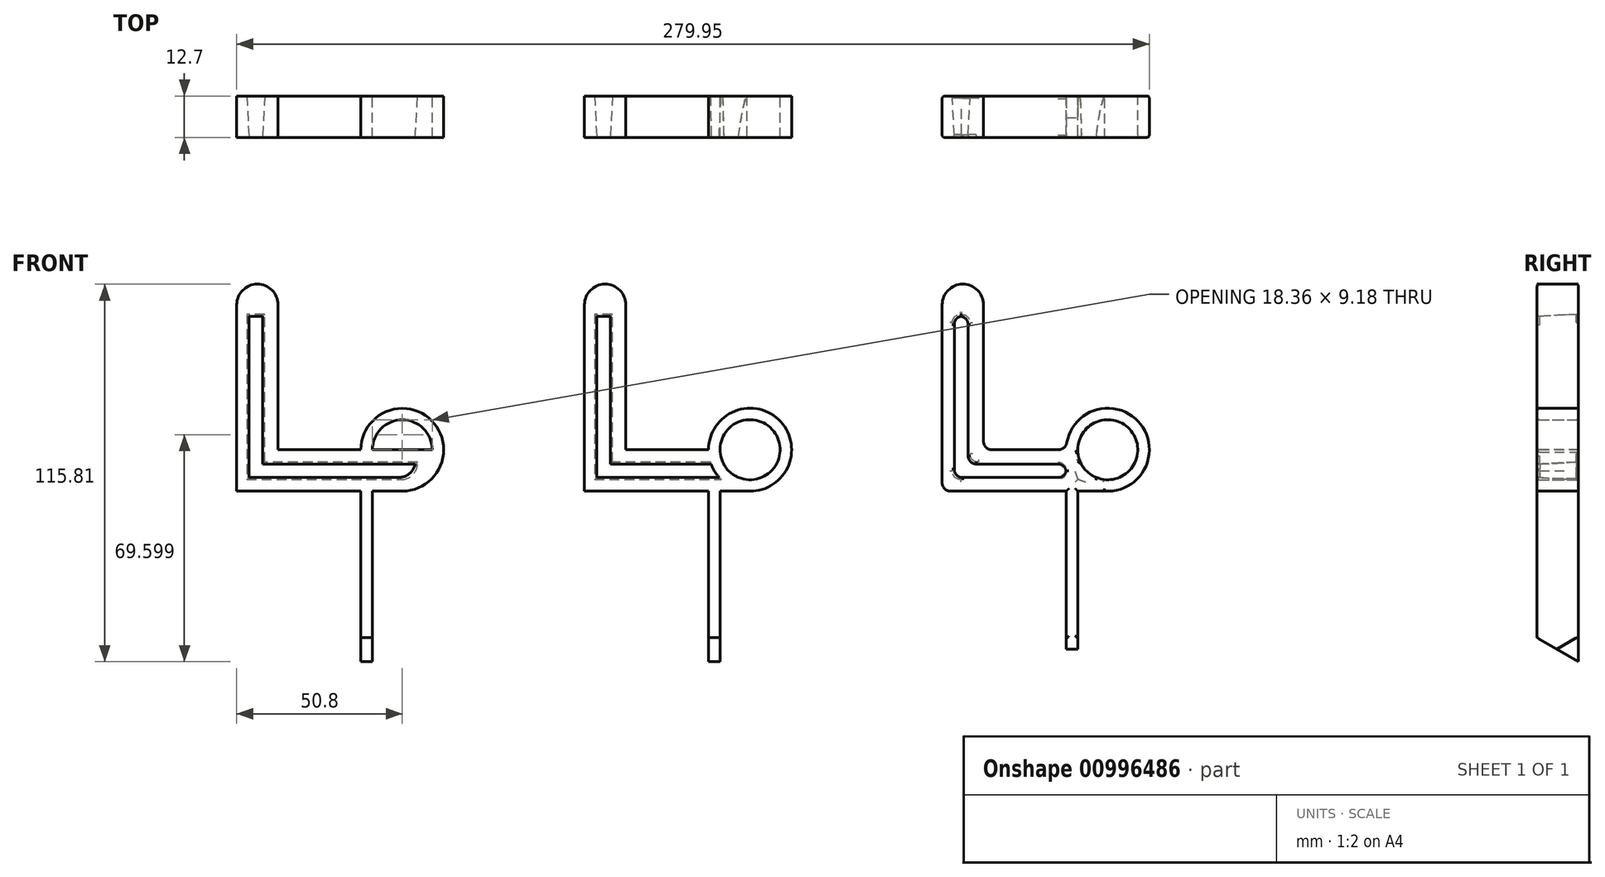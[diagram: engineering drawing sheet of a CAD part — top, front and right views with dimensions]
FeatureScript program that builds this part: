
annotation { "Feature Type Name" : "Feature", "Feature Type Description" : "" }
export const myFeature = defineFeature(function(context is Context, id is Id, definition is map)
    precondition{}
    {
        {
            var Q0;
            Q0=qCreatedBy(makeId("Front.planeOp"),FACE);
            var sketch = newSketch(context, id + "F0", { "sketchPlane" : qUnion([Q0])});
            skLineSegment(sketch, "E0", {"start": v(0, 63.5) * mm, "end": v(0, 0) * mm});
            skLineSegment(sketch, "E1", {"start": v(0, 0) * mm, "end": v(63.5, 0) * mm});
            skLineSegment(sketch, "E2", {"start": v(0, 63.5) * mm, "end": v(12.7, 63.5) * mm});
            skLineSegment(sketch, "E3", {"start": v(12.7, 63.5) * mm, "end": v(12.7, 12.7) * mm});
            skLineSegment(sketch, "E4", {"start": v(12.7, 12.7) * mm, "end": v(63.5, 12.7) * mm});
            skLineSegment(sketch, "E5", {"start": v(63.5, 12.7) * mm, "end": v(63.5, 0) * mm});
            skSolve(sketch);
        }
        {
            var Q0;
            Q0 = qSketchRegion(id + "F0", true);
            extrude(context, id + "F1", {"entities" : qUnion([Q0]), "depth" : 12.7 * mm, "offsetDistance" : 25.4 * mm});
        }
        {
            var Q0;
            Q0=qCreatedBy(makeId("Front.planeOp"),FACE);
            var sketch = newSketch(context, id + "F2", { "sketchPlane" : qUnion([Q0])});
            skArc(sketch, "E6", {"start": v(63.5, 12.7) * mm, "mid": v(50.8, 25.37) * mm, "end": v(38.1, 12.7) * mm});
            skArc(sketch, "E7", {"start": v(38.1, 12.7) * mm, "mid": v(50.8, 0) * mm, "end": v(63.5, 12.7) * mm});
            skCircle(sketch, "E8", {"center": v(50.8, 12.7) * mm, "radius": 9.18 * mm});
            skSolve(sketch);
        }
        {
            var Q0;
            Q0 = qSketchRegion(id + "F2", true);
            var Q1;
            Q1=makeQuery(id+"F1.opExtrude","CAP_VERTEX",VERTEX,{"disambiguationData":[OSD([sQuery(id+"F0.wireOp",EDGE,"E4"),sQuery(id+"F0.wireOp",EDGE,"E5")])],"isStart":false});
            extrude(context, id + "F3", {"entities" : qUnion([Q0]), "operationType" : NewBodyOperationType.ADD, "endBound" : BoundingType.UP_TO_VERTEX, "depth" : 25.4 * mm, "endBoundEntityVertex" : qUnion([Q1]), "offsetDistance" : 25.4 * mm});
        }
        {
            var Q0;
            Q0=qCreatedBy(makeId("Front.planeOp"),FACE);
            var sketch = newSketch(context, id + "F4", { "sketchPlane" : qUnion([Q0])});
            skLineSegment(sketch, "E9.bottom", {"start": v(38.1, 12.7) * mm, "end": v(41.62, 12.7) * mm});
            skLineSegment(sketch, "E9.top", {"start": v(38.1, -57.68) * mm, "end": v(41.62, -57.68) * mm});
            skLineSegment(sketch, "E9.left", {"start": v(38.1, 12.7) * mm, "end": v(38.1, -57.68) * mm});
            skLineSegment(sketch, "E9.right", {"start": v(41.62, 12.7) * mm, "end": v(41.62, -57.68) * mm});
            skSolve(sketch);
        }
        {
            var Q0;
            Q0=makeQuery(id+"F4.imprint","IMPRINT",FACE,{"disambiguationData":[TD([[makeQuery(id+"F4.imprint","IMPRINT",EDGE,{"derivedFrom":sQuery(id+"F4.wireOp",EDGE,"E9.bottom")}),-1.0]])]});
            var Q1;
            Q1=makeQuery(id+"F3.opExtrude","CAP_VERTEX",VERTEX,{"disambiguationData":[OSD([sQuery(id+"F2.wireOp",EDGE,"E6"),sQuery(id+"F2.wireOp",EDGE,"E7")]),OD(1.0)],"isStart":false});
            extrude(context, id + "F5", {"entities" : qUnion([Q0]), "operationType" : NewBodyOperationType.ADD, "endBound" : BoundingType.UP_TO_VERTEX, "depth" : 25.4 * mm, "endBoundEntityVertex" : qUnion([Q1]), "offsetDistance" : 25.4 * mm});
        }
        {
            var Q0;
            Q0=makeQuery(id+"F1.opExtrude","SWEPT_EDGE",EDGE,{"disambiguationData":[OSD([sQuery(id+"F0.wireOp",EDGE,"E2"),sQuery(id+"F0.wireOp",EDGE,"E3")])]});
            var Q1;
            Q1=makeQuery(id+"F1.opExtrude","SWEPT_EDGE",EDGE,{"disambiguationData":[OSD([sQuery(id+"F0.wireOp",EDGE,"E0"),sQuery(id+"F0.wireOp",EDGE,"E2")])]});
            fillet(context, id + "F6", {"entities" : qUnion([Q0, Q1]), "radius" : 6.35 * mm, "tangentPropagation" : true, "allowEdgeOverflow" : false});
        }
        {
            var Q0;
            Q0=makeQuery(id+"F1.opExtrude","SWEPT_EDGE",EDGE,{"disambiguationData":[OSD([sQuery(id+"F0.wireOp",EDGE,"E1"),sQuery(id+"F0.wireOp",EDGE,"E5")])]});
            fillet(context, id + "F7", {"entities" : qUnion([Q0]), "radius" : 12.7 * mm, "tangentPropagation" : true, "allowEdgeOverflow" : false});
        }
        {
            var Q0;
            Q0=makeQuery(id+"F5.opExtrude","CAP_EDGE",EDGE,{"disambiguationData":[OSD([sQuery(id+"F4.wireOp",EDGE,"E9.top")])],"isStart":false});
            chamfer(context, id + "F8", {"entities" : qUnion([Q0]), "chamferType" : ChamferType.OFFSET_ANGLE, "width" : 12.7 * mm, "oppositeDirection" : false, "angle" : 60 * degree, "tangentPropagation" : true});
        }
        {
            var Q0;
            Q0=makeQuery(id+"F5.boolean.opBoolean","MERGE",FACE,{"derivedFrom":[makeQuery(id+"F3.boolean.opBoolean","MERGE",FACE,{"derivedFrom":[makeQuery(id+"F1.opExtrude","CAP_FACE",FACE,{"disambiguationData":[OSD([sQuery(id+"F0.wireOp",EDGE,"E0"),sQuery(id+"F0.wireOp",EDGE,"E1"),sQuery(id+"F0.wireOp",EDGE,"E2"),sQuery(id+"F0.wireOp",EDGE,"E3"),sQuery(id+"F0.wireOp",EDGE,"E4"),sQuery(id+"F0.wireOp",EDGE,"E5")])],"isStart":false}),makeQuery(id+"F3.opExtrude","CAP_FACE",FACE,{"disambiguationData":[OSD([sQuery(id+"F2.wireOp",EDGE,"E6"),sQuery(id+"F2.wireOp",EDGE,"E7"),sQuery(id+"F2.wireOp",EDGE,"E8")])],"isStart":false})]}),makeQuery(id+"F5.opExtrude","CAP_FACE",FACE,{"disambiguationData":[OSD([sQuery(id+"F4.wireOp",EDGE,"E9.bottom"),sQuery(id+"F4.wireOp",EDGE,"E9.top"),sQuery(id+"F4.wireOp",EDGE,"E9.left"),sQuery(id+"F4.wireOp",EDGE,"E9.right")])],"isStart":false})]});
            var sketch = newSketch(context, id + "F9", { "sketchPlane" : qUnion([Q0])});
            skLineSegment(sketch, "E10", {"start": v(7.9, 53.6) * mm, "end": v(7.9, 8.26) * mm});
            skLineSegment(sketch, "E11", {"start": v(7.9, 8.26) * mm, "end": v(54.83, 8.26) * mm});
            skLineSegment(sketch, "E12", {"start": v(54.83, 8.26) * mm, "end": v(54.83, 4.2) * mm});
            skLineSegment(sketch, "E13", {"start": v(54.83, 4.2) * mm, "end": v(3.75, 4.2) * mm});
            skLineSegment(sketch, "E14", {"start": v(3.75, 4.2) * mm, "end": v(3.75, 53.6) * mm});
            skLineSegment(sketch, "E15", {"start": v(3.75, 53.6) * mm, "end": v(7.9, 53.6) * mm});
            skPoint(sketch, "E16.visualSharp", {"position": v(7.9, 53.6) * mm});
            skLineSegment(sketch, "E16.filletArc", {"start": v(7.9, 53.6) * mm, "end": v(7.9, 53.6) * mm});
            skSolve(sketch);
        }
        {
            var Q0;
            Q0 = qSketchRegion(id + "F9", true);
            extrude(context, id + "F10", {"entities" : qUnion([Q0]), "operationType" : NewBodyOperationType.REMOVE, "oppositeDirection" : true, "depth" : 102.36 * mm, "offsetDistance" : 25.4 * mm, "hasDraft" : true, "draftAngle" : 3 * degree});
        }
        {
            var Q0;
            Q0=makeQuery(id+"F10.boolean.opBoolean","COPY",EDGE,{"derivedFrom":makeQuery(id+"F10.opExtrude","SWEPT_EDGE",EDGE,{"disambiguationData":[OSD([sQuery(id+"F9.wireOp",EDGE,"E12"),sQuery(id+"F9.wireOp",EDGE,"E13")])]})});
            fillet(context, id + "F11", {"entities" : qUnion([Q0]), "radius" : 5.08 * mm, "tangentPropagation" : true, "allowEdgeOverflow" : false});
        }
        {
            var Q0;
            Q0=makeQuery(id+"F1.opExtrude","SWEPT_BODY",BODY,{"disambiguationData":[OSD([sQuery(id+"F0.wireOp",EDGE,"E0"),sQuery(id+"F0.wireOp",EDGE,"E1"),sQuery(id+"F0.wireOp",EDGE,"E2"),sQuery(id+"F0.wireOp",EDGE,"E3"),sQuery(id+"F0.wireOp",EDGE,"E4"),sQuery(id+"F0.wireOp",EDGE,"E5")])]});
            transform(context, id + "F12", {"entities" : qUnion([Q0]), "transformType" : TransformType.TRANSLATION_3D, "dx" : 106.68 * mm, "dy" : 0 * mm, "dz" : 0 * mm, "makeCopy" : true});
        }
        {
            var Q0;
            Q0=qCreatedBy(makeId("Front.planeOp"),FACE);
            var sketch = newSketch(context, id + "F13", { "sketchPlane" : qUnion([Q0])});
            skCircle(sketch, "E17", {"center": v(157.48, 12.7) * mm, "radius": 9.21 * mm});
            skSolve(sketch);
        }
        {
            var Q0;
            Q0 = qSketchRegion(id + "F13", true);
            extrude(context, id + "F14", {"entities" : qUnion([Q0]), "operationType" : NewBodyOperationType.REMOVE, "depth" : 103.12 * mm, "offsetDistance" : 25.4 * mm});
        }
        {
            var Q0;
            Q0=makeQuery(id+"F12.opPattern","COPY",FACE,{"derivedFrom":makeQuery(id+"F5.boolean.opBoolean","MERGE",FACE,{"derivedFrom":[makeQuery(id+"F3.boolean.opBoolean","MERGE",FACE,{"derivedFrom":[makeQuery(id+"F1.opExtrude","CAP_FACE",FACE,{"disambiguationData":[OSD([sQuery(id+"F0.wireOp",EDGE,"E0"),sQuery(id+"F0.wireOp",EDGE,"E1"),sQuery(id+"F0.wireOp",EDGE,"E2"),sQuery(id+"F0.wireOp",EDGE,"E3"),sQuery(id+"F0.wireOp",EDGE,"E4"),sQuery(id+"F0.wireOp",EDGE,"E5")])],"isStart":false}),makeQuery(id+"F3.opExtrude","CAP_FACE",FACE,{"disambiguationData":[OSD([sQuery(id+"F2.wireOp",EDGE,"E6"),sQuery(id+"F2.wireOp",EDGE,"E7"),sQuery(id+"F2.wireOp",EDGE,"E8")])],"isStart":false})]}),makeQuery(id+"F5.opExtrude","CAP_FACE",FACE,{"disambiguationData":[OSD([sQuery(id+"F4.wireOp",EDGE,"E9.bottom"),sQuery(id+"F4.wireOp",EDGE,"E9.top"),sQuery(id+"F4.wireOp",EDGE,"E9.left"),sQuery(id+"F4.wireOp",EDGE,"E9.right")])],"isStart":false})]}),"instanceName":"1"});
            var sketch = newSketch(context, id + "F15", { "sketchPlane" : qUnion([Q0])});
            skCircle(sketch, "E18", {"center": v(157.48, 12.7) * mm, "radius": 12.74 * mm});
            skCircle(sketch, "E19", {"center": v(157.48, 12.7) * mm, "radius": 9.23 * mm});
            skSolve(sketch);
        }
        {
            var Q0;
            Q0 = qSketchRegion(id + "F15", true);
            extrude(context, id + "F16", {"entities" : qUnion([Q0]), "operationType" : NewBodyOperationType.ADD, "oppositeDirection" : true, "depth" : 12.7 * mm, "offsetDistance" : 25.4 * mm});
        }
        {
            var Q0;
            Q0=makeQuery(id+"F12.opPattern","COPY",BODY,{"derivedFrom":makeQuery(id+"F1.opExtrude","SWEPT_BODY",BODY,{"disambiguationData":[OSD([sQuery(id+"F0.wireOp",EDGE,"E0"),sQuery(id+"F0.wireOp",EDGE,"E1"),sQuery(id+"F0.wireOp",EDGE,"E2"),sQuery(id+"F0.wireOp",EDGE,"E3"),sQuery(id+"F0.wireOp",EDGE,"E4"),sQuery(id+"F0.wireOp",EDGE,"E5")])]}),"instanceName":"1"});
            transform(context, id + "F17", {"entities" : qUnion([Q0]), "transformType" : TransformType.TRANSLATION_3D, "dx" : 109.73 * mm, "dy" : 0 * mm, "dz" : 0 * mm, "makeCopy" : true});
        }
        {
            var Q0;
            Q0=makeQuery(id+"F17.opPattern","COPY",FACE,{"derivedFrom":makeQuery(id+"F16.boolean.opBoolean","MERGE",FACE,{"derivedFrom":[makeQuery(id+"F12.opPattern","COPY",FACE,{"derivedFrom":makeQuery(id+"F5.boolean.opBoolean","MERGE",FACE,{"derivedFrom":[makeQuery(id+"F3.boolean.opBoolean","MERGE",FACE,{"derivedFrom":[makeQuery(id+"F1.opExtrude","CAP_FACE",FACE,{"disambiguationData":[OSD([sQuery(id+"F0.wireOp",EDGE,"E0"),sQuery(id+"F0.wireOp",EDGE,"E1"),sQuery(id+"F0.wireOp",EDGE,"E2"),sQuery(id+"F0.wireOp",EDGE,"E3"),sQuery(id+"F0.wireOp",EDGE,"E4"),sQuery(id+"F0.wireOp",EDGE,"E5")])],"isStart":false}),makeQuery(id+"F3.opExtrude","CAP_FACE",FACE,{"disambiguationData":[OSD([sQuery(id+"F2.wireOp",EDGE,"E6"),sQuery(id+"F2.wireOp",EDGE,"E7"),sQuery(id+"F2.wireOp",EDGE,"E8")])],"isStart":false})]}),makeQuery(id+"F5.opExtrude","CAP_FACE",FACE,{"disambiguationData":[OSD([sQuery(id+"F4.wireOp",EDGE,"E9.bottom"),sQuery(id+"F4.wireOp",EDGE,"E9.top"),sQuery(id+"F4.wireOp",EDGE,"E9.left"),sQuery(id+"F4.wireOp",EDGE,"E9.right")])],"isStart":false})]}),"instanceName":"1"}),makeQuery(id+"F16.opExtrude","CAP_FACE",FACE,{"disambiguationData":[OSD([sQuery(id+"F15.wireOp",EDGE,"E18"),sQuery(id+"F15.wireOp",EDGE,"E19")])],"isStart":true})]}),"instanceName":"1"});
            var sketch = newSketch(context, id + "F18", { "sketchPlane" : qUnion([Q0])});
            skLineSegment(sketch, "E20.bottom", {"start": v(258.03, 0) * mm, "end": v(254.47, 0) * mm});
            skLineSegment(sketch, "E20.top", {"start": v(258.03, 12.7) * mm, "end": v(254.47, 12.7) * mm});
            skLineSegment(sketch, "E20.left", {"start": v(258.03, 0) * mm, "end": v(258.03, 12.7) * mm});
            skLineSegment(sketch, "E20.right", {"start": v(254.47, 0) * mm, "end": v(254.47, 12.7) * mm});
            skSolve(sketch);
        }
        {
            var Q0;
            Q0 = qSketchRegion(id + "F18", true);
            extrude(context, id + "F19", {"entities" : qUnion([Q0]), "operationType" : NewBodyOperationType.ADD, "oppositeDirection" : true, "depth" : 12.7 * mm, "offsetDistance" : 25.4 * mm});
        }
        {
            var Q0;
            {var subQ0=sQuery(id+"F4.wireOp",EDGE,"E9.top");Q0=makeQuery(id+"F17.opPattern","COPY",EDGE,{"derivedFrom":makeQuery(id+"F12.opPattern","COPY",EDGE,{"derivedFrom":makeQuery(id+"F8.opChamfer","BLEND_EDGE",EDGE,{"blendedFrom":[makeQuery(id+"F5.opExtrude","CAP_EDGE",EDGE,{"disambiguationData":[OSD([subQ0])],"isStart":false}),makeQuery(id+"F5.boolean.opBoolean","MERGE",FACE,{"derivedFrom":[makeQuery(id+"F3.boolean.opBoolean","MERGE",FACE,{"derivedFrom":[makeQuery(id+"F1.opExtrude","CAP_FACE",FACE,{"disambiguationData":[OSD([sQuery(id+"F0.wireOp",EDGE,"E0"),sQuery(id+"F0.wireOp",EDGE,"E1"),sQuery(id+"F0.wireOp",EDGE,"E2"),sQuery(id+"F0.wireOp",EDGE,"E3"),sQuery(id+"F0.wireOp",EDGE,"E4"),sQuery(id+"F0.wireOp",EDGE,"E5")])],"isStart":true}),makeQuery(id+"F3.opExtrude","CAP_FACE",FACE,{"disambiguationData":[OSD([sQuery(id+"F2.wireOp",EDGE,"E6"),sQuery(id+"F2.wireOp",EDGE,"E7"),sQuery(id+"F2.wireOp",EDGE,"E8")])],"isStart":true})]}),makeQuery(id+"F5.opExtrude","CAP_FACE",FACE,{"disambiguationData":[OSD([sQuery(id+"F4.wireOp",EDGE,"E9.bottom"),subQ0,sQuery(id+"F4.wireOp",EDGE,"E9.left"),sQuery(id+"F4.wireOp",EDGE,"E9.right")])],"isStart":true})]})],"blendedInto":[makeQuery(id+"F5.boolean.opBoolean","MERGE",FACE,{"derivedFrom":[makeQuery(id+"F3.boolean.opBoolean","MERGE",FACE,{"derivedFrom":[makeQuery(id+"F1.opExtrude","CAP_FACE",FACE,{"disambiguationData":[OSD([sQuery(id+"F0.wireOp",EDGE,"E0"),sQuery(id+"F0.wireOp",EDGE,"E1"),sQuery(id+"F0.wireOp",EDGE,"E2"),sQuery(id+"F0.wireOp",EDGE,"E3"),sQuery(id+"F0.wireOp",EDGE,"E4"),sQuery(id+"F0.wireOp",EDGE,"E5")])],"isStart":true}),makeQuery(id+"F3.opExtrude","CAP_FACE",FACE,{"disambiguationData":[OSD([sQuery(id+"F2.wireOp",EDGE,"E6"),sQuery(id+"F2.wireOp",EDGE,"E7"),sQuery(id+"F2.wireOp",EDGE,"E8")])],"isStart":true})]}),makeQuery(id+"F5.opExtrude","CAP_FACE",FACE,{"disambiguationData":[OSD([sQuery(id+"F4.wireOp",EDGE,"E9.bottom"),subQ0,sQuery(id+"F4.wireOp",EDGE,"E9.left"),sQuery(id+"F4.wireOp",EDGE,"E9.right")])],"isStart":true})]})]}),"instanceName":"1"}),"instanceName":"1"});}
            chamfer(context, id + "F20", {"entities" : qUnion([Q0]), "chamferType" : ChamferType.OFFSET_ANGLE, "width" : 7.62 * mm, "oppositeDirection" : false, "angle" : 60 * degree, "tangentPropagation" : true});
        }
        {
            var Q0;
            Q0=makeQuery(id+"F17.opPattern","COPY",EDGE,{"derivedFrom":makeQuery(id+"F12.opPattern","COPY",EDGE,{"derivedFrom":makeQuery(id+"F10.boolean.opBoolean","COPY",EDGE,{"derivedFrom":makeQuery(id+"F10.opExtrude","SWEPT_EDGE",EDGE,{"disambiguationData":[OSD([sQuery(id+"F9.wireOp",EDGE,"E14"),sQuery(id+"F9.wireOp",EDGE,"E15")])]})}),"instanceName":"1"}),"instanceName":"1"});
            var Q1;
            Q1=makeQuery(id+"F17.opPattern","COPY",EDGE,{"derivedFrom":makeQuery(id+"F12.opPattern","COPY",EDGE,{"derivedFrom":makeQuery(id+"F10.boolean.opBoolean","COPY",EDGE,{"derivedFrom":makeQuery(id+"F10.opExtrude","SWEPT_EDGE",EDGE,{"disambiguationData":[OSD([sQuery(id+"F9.wireOp",EDGE,"E10"),sQuery(id+"F9.wireOp",EDGE,"E15")])]})}),"instanceName":"1"}),"instanceName":"1"});
            var Q2;
            Q2=makeQuery(id+"F17.opPattern","COPY",EDGE,{"derivedFrom":makeQuery(id+"F12.opPattern","COPY",EDGE,{"derivedFrom":makeQuery(id+"F10.boolean.opBoolean","COPY",EDGE,{"derivedFrom":makeQuery(id+"F10.opExtrude","SWEPT_EDGE",EDGE,{"disambiguationData":[OSD([sQuery(id+"F9.wireOp",EDGE,"E10"),sQuery(id+"F9.wireOp",EDGE,"E11")])]})}),"instanceName":"1"}),"instanceName":"1"});
            var Q3;
            Q3=makeQuery(id+"F19.boolean.opBoolean","INTERSECT",EDGE,{"derivedFrom":[makeQuery(id+"F17.opPattern","COPY",FACE,{"derivedFrom":makeQuery(id+"F16.boolean.opBoolean","SPLIT",FACE,{"disambiguationData":[TD([makeQuery(id+"F12.opPattern","COPY",FACE,{"derivedFrom":makeQuery(id+"F10.boolean.opBoolean","COPY",FACE,{"derivedFrom":makeQuery(id+"F10.opExtrude","SWEPT_FACE",FACE,{"disambiguationData":[OSD([sQuery(id+"F9.wireOp",EDGE,"E10")])]})}),"instanceName":"1"})])],"derivedFrom":makeQuery(id+"F12.opPattern","COPY",FACE,{"derivedFrom":makeQuery(id+"F10.boolean.opBoolean","COPY",FACE,{"derivedFrom":makeQuery(id+"F10.opExtrude","SWEPT_FACE",FACE,{"disambiguationData":[OSD([sQuery(id+"F9.wireOp",EDGE,"E11")])]})}),"instanceName":"1"})}),"instanceName":"1"}),makeQuery(id+"F19.opExtrude","SWEPT_FACE",FACE,{"disambiguationData":[OSD([sQuery(id+"F18.wireOp",EDGE,"E20.right")])]})]});
            var Q4;
            Q4=makeQuery(id+"F19.boolean.opBoolean","INTERSECT",EDGE,{"derivedFrom":[makeQuery(id+"F17.opPattern","COPY",FACE,{"derivedFrom":makeQuery(id+"F16.boolean.opBoolean","SPLIT",FACE,{"disambiguationData":[TD([makeQuery(id+"F12.opPattern","COPY",FACE,{"derivedFrom":makeQuery(id+"F10.boolean.opBoolean","COPY",FACE,{"derivedFrom":makeQuery(id+"F10.opExtrude","SWEPT_FACE",FACE,{"disambiguationData":[OSD([sQuery(id+"F9.wireOp",EDGE,"E14")])]})}),"instanceName":"1"})])],"derivedFrom":makeQuery(id+"F12.opPattern","COPY",FACE,{"derivedFrom":makeQuery(id+"F10.boolean.opBoolean","COPY",FACE,{"derivedFrom":makeQuery(id+"F10.opExtrude","SWEPT_FACE",FACE,{"disambiguationData":[OSD([sQuery(id+"F9.wireOp",EDGE,"E13")])]})}),"instanceName":"1"})}),"instanceName":"1"}),makeQuery(id+"F19.opExtrude","SWEPT_FACE",FACE,{"disambiguationData":[OSD([sQuery(id+"F18.wireOp",EDGE,"E20.right")])]})]});
            var Q5;
            Q5=makeQuery(id+"F17.opPattern","COPY",EDGE,{"derivedFrom":makeQuery(id+"F12.opPattern","COPY",EDGE,{"derivedFrom":makeQuery(id+"F10.boolean.opBoolean","COPY",EDGE,{"derivedFrom":makeQuery(id+"F10.opExtrude","SWEPT_EDGE",EDGE,{"disambiguationData":[OSD([sQuery(id+"F9.wireOp",EDGE,"E13"),sQuery(id+"F9.wireOp",EDGE,"E14")])]})}),"instanceName":"1"}),"instanceName":"1"});
            var Q6;
            {var subQ1=sQuery(id+"F0.wireOp",EDGE,"E3");var subQ3=sQuery(id+"F0.wireOp",EDGE,"E4");Q6=makeQuery(id+"F17.opPattern","COPY",EDGE,{"derivedFrom":makeQuery(id+"F16.boolean.opBoolean","INTERSECT",EDGE,{"derivedFrom":[makeQuery(id+"F12.opPattern","COPY",FACE,{"derivedFrom":makeQuery(id+"F3.boolean.opBoolean","SPLIT",FACE,{"disambiguationData":[TD([makeQuery(id+"F1.opExtrude","SWEPT_FACE",FACE,{"disambiguationData":[OSD([subQ1])]})])],"derivedFrom":makeQuery(id+"F1.opExtrude","SWEPT_FACE",FACE,{"disambiguationData":[OSD([subQ3])]})}),"instanceName":"1"}),makeQuery(id+"F16.opExtrude","SWEPT_FACE",FACE,{"disambiguationData":[OSD([sQuery(id+"F15.wireOp",EDGE,"E18")])]})]}),"instanceName":"1"});}
            var Q7;
            Q7=makeQuery(id+"F17.opPattern","COPY",EDGE,{"derivedFrom":makeQuery(id+"F12.opPattern","COPY",EDGE,{"derivedFrom":makeQuery(id+"F1.opExtrude","SWEPT_EDGE",EDGE,{"disambiguationData":[OSD([sQuery(id+"F0.wireOp",EDGE,"E3"),sQuery(id+"F0.wireOp",EDGE,"E4")])]}),"instanceName":"1"}),"instanceName":"1"});
            var Q8;
            Q8=makeQuery(id+"F17.opPattern","COPY",EDGE,{"derivedFrom":makeQuery(id+"F12.opPattern","COPY",EDGE,{"derivedFrom":makeQuery(id+"F1.opExtrude","SWEPT_EDGE",EDGE,{"disambiguationData":[OSD([sQuery(id+"F0.wireOp",EDGE,"E0"),sQuery(id+"F0.wireOp",EDGE,"E1")])]}),"instanceName":"1"}),"instanceName":"1"});
            fillet(context, id + "F21", {"entities" : qUnion([Q0, Q1, Q2, Q3, Q4, Q5, Q6, Q7, Q8]), "radius" : 2.54 * mm, "tangentPropagation" : true, "allowEdgeOverflow" : false});
        }
        {
            var Q0;
            Q0=makeQuery(id+"F19.boolean.opBoolean","MERGE",FACE,{"derivedFrom":[makeQuery(id+"F17.opPattern","COPY",FACE,{"derivedFrom":makeQuery(id+"F16.boolean.opBoolean","MERGE",FACE,{"derivedFrom":[makeQuery(id+"F12.opPattern","COPY",FACE,{"derivedFrom":makeQuery(id+"F5.boolean.opBoolean","MERGE",FACE,{"derivedFrom":[makeQuery(id+"F3.boolean.opBoolean","MERGE",FACE,{"derivedFrom":[makeQuery(id+"F1.opExtrude","CAP_FACE",FACE,{"disambiguationData":[OSD([sQuery(id+"F0.wireOp",EDGE,"E0"),sQuery(id+"F0.wireOp",EDGE,"E1"),sQuery(id+"F0.wireOp",EDGE,"E2"),sQuery(id+"F0.wireOp",EDGE,"E3"),sQuery(id+"F0.wireOp",EDGE,"E4"),sQuery(id+"F0.wireOp",EDGE,"E5")])],"isStart":false}),makeQuery(id+"F3.opExtrude","CAP_FACE",FACE,{"disambiguationData":[OSD([sQuery(id+"F2.wireOp",EDGE,"E6"),sQuery(id+"F2.wireOp",EDGE,"E7"),sQuery(id+"F2.wireOp",EDGE,"E8")])],"isStart":false})]}),makeQuery(id+"F5.opExtrude","CAP_FACE",FACE,{"disambiguationData":[OSD([sQuery(id+"F4.wireOp",EDGE,"E9.bottom"),sQuery(id+"F4.wireOp",EDGE,"E9.top"),sQuery(id+"F4.wireOp",EDGE,"E9.left"),sQuery(id+"F4.wireOp",EDGE,"E9.right")])],"isStart":false})]}),"instanceName":"1"}),makeQuery(id+"F16.opExtrude","CAP_FACE",FACE,{"disambiguationData":[OSD([sQuery(id+"F15.wireOp",EDGE,"E18"),sQuery(id+"F15.wireOp",EDGE,"E19")])],"isStart":true})]}),"instanceName":"1"}),makeQuery(id+"F19.opExtrude","CAP_FACE",FACE,{"disambiguationData":[OSD([sQuery(id+"F18.wireOp",EDGE,"E20.bottom"),sQuery(id+"F18.wireOp",EDGE,"E20.top"),sQuery(id+"F18.wireOp",EDGE,"E20.left"),sQuery(id+"F18.wireOp",EDGE,"E20.right")])],"isStart":true})]});
            var Q1;
            Q1=makeQuery(id+"F19.boolean.opBoolean","MERGE",FACE,{"derivedFrom":[makeQuery(id+"F17.opPattern","COPY",FACE,{"derivedFrom":makeQuery(id+"F16.boolean.opBoolean","MERGE",FACE,{"derivedFrom":[makeQuery(id+"F12.opPattern","COPY",FACE,{"derivedFrom":makeQuery(id+"F5.boolean.opBoolean","MERGE",FACE,{"derivedFrom":[makeQuery(id+"F3.boolean.opBoolean","MERGE",FACE,{"derivedFrom":[makeQuery(id+"F1.opExtrude","CAP_FACE",FACE,{"disambiguationData":[OSD([sQuery(id+"F0.wireOp",EDGE,"E0"),sQuery(id+"F0.wireOp",EDGE,"E1"),sQuery(id+"F0.wireOp",EDGE,"E2"),sQuery(id+"F0.wireOp",EDGE,"E3"),sQuery(id+"F0.wireOp",EDGE,"E4"),sQuery(id+"F0.wireOp",EDGE,"E5")])],"isStart":true}),makeQuery(id+"F3.opExtrude","CAP_FACE",FACE,{"disambiguationData":[OSD([sQuery(id+"F2.wireOp",EDGE,"E6"),sQuery(id+"F2.wireOp",EDGE,"E7"),sQuery(id+"F2.wireOp",EDGE,"E8")])],"isStart":true})]}),makeQuery(id+"F5.opExtrude","CAP_FACE",FACE,{"disambiguationData":[OSD([sQuery(id+"F4.wireOp",EDGE,"E9.bottom"),sQuery(id+"F4.wireOp",EDGE,"E9.top"),sQuery(id+"F4.wireOp",EDGE,"E9.left"),sQuery(id+"F4.wireOp",EDGE,"E9.right")])],"isStart":true})]}),"instanceName":"1"}),makeQuery(id+"F16.opExtrude","CAP_FACE",FACE,{"disambiguationData":[OSD([sQuery(id+"F15.wireOp",EDGE,"E18"),sQuery(id+"F15.wireOp",EDGE,"E19")])],"isStart":false})]}),"instanceName":"1"}),makeQuery(id+"F19.opExtrude","CAP_FACE",FACE,{"disambiguationData":[OSD([sQuery(id+"F18.wireOp",EDGE,"E20.bottom"),sQuery(id+"F18.wireOp",EDGE,"E20.top"),sQuery(id+"F18.wireOp",EDGE,"E20.left"),sQuery(id+"F18.wireOp",EDGE,"E20.right")])],"isStart":false})]});
            fillet(context, id + "F22", {"entities" : qUnion([Q0, Q1]), "radius" : 0.76 * mm, "tangentPropagation" : true, "allowEdgeOverflow" : false});
        }
    });
